# Revit family: FlushPlateControlPanel-ToiletCisterns-ProPhotocelled-Vitra-VitrAProSeries_748-1420
name_source: partatom
category: Plumbing Fixtures
revit_build: Autodesk Revit 2017 (Build: 20160225_1515(x64)
units: mm (PartAtom-declared; Revit-internal decimal feet)

## family parameters
Cut with Voids When Loaded = No
Host = Face
OmniClass Number = 23.45.00.00
OmniClass Title = Sanitary, Laundry, and Cleaning Equipment
Part Type = Normal
Room Calculation Point = No
Round Connector Dimension = Use Diameter
Shared = Yes

## types (6) — shared parameters
BIMobject category = Toilet Cisterns
Brand = VitrA
CW Connection = No
Design country = Turkey
HW Connection = No
IFC Classification = Sanitary Terminal
Main Material = Metal
Manufacturer = Vitra
Manufacturer name = Vitra
Masterformat 2014 Code = 22 00 00
Masterformat 2014 Description = Plumbing
Mounting type = Wall Mounted
NBS Referans Code = 31-75
NBS Referans Description = Sanitary Accessories
Nominal Depth (mm) = 10 mm  [stored 0.0328084 ft]
Nominal Height (mm) = 160 mm  [stored 0.524934 ft]
Nominal Width (mm) = 240 mm  [stored 0.787402 ft]
OmniClass Code = 23-31 00 00
OmniClass Description = Plumbing Specific Products and Equipment
Primary Material = Matte Black
Product Properties = Vitra Pro Control Panel
Product certification = https://www.vitraglobal.com
Product family = VitrA Pro
Product group = WC Cisterns Control Panel
UNSPSC Description = Plumbing connectors
URL = https://www.vitra.com.tr
Uniclass 1.4 Code = L71111
Uniclass 1.4 Description = Packaged plumbing units
Uniclass 2.0 Code = PR-31-75
Uniclass 2.0 Description = Sanitary Accessories
Uniclass 2015 Code = Pr_40_20_76
Uniclass 2015 Name = Sanitary accessories
Uniformat II Code = D20
Uniformat II Description = PLUMBING
Vent Connection = No
Warranty Period (Year) = 2 Years
Waste Connection = No
Weight Net (kg) = 0.95
Youtube = https://www.youtube.com
zero-valued in all types: Default Elevation

## per-type parameters (varying)
| type | Article No. (default) | Coating Material | Color | Description | Model | Product SKU | Product url | Technical description |
| FlushPlateControlPanel-ToiletCisterns-ProPhotocelled-Vitra-VitrAProSeries_748-1420IND | 748-1420IND | Gold | Gold | VitrA WC Cisterns Control Panel - Pro Photocelled Control Panel - Electronic- Gold - Compatible with Slim Frames (748-frames) | 748-1420IND | 748-1420IND | https://www.vitra-india.com | https://www.vitra-india.com |
| FlushPlateControlPanel-ToiletCisterns-ProPhotocelled-Vitra-VitrAProSeries_748-1420 | 748-1420 | Gold | Gold | VitrA WC Cisterns Control Panel - Pro Photocelled Control Panel - Electronic- Gold - Compatible with Slim Frames (748-frames) | 748-1420 | 748-1420 | https://www.vitra.com.tr | https://www.vitra.com.tr |
| FlushPlateControlPanel-ToiletCisterns-ProPhotocelled-Vitra-VitrAProSeries_748-1440 | 748-1440 | Brushed Chrome | Brushed Chrome | VitrA WC Cisterns Control Panel - Pro Photocelled Control Panel - Electronic- Brushed Chrome- Compatible with Slim Frames (748-frames) | 748-1440 | 748-1440 | https://www.vitra.com.tr | https://www.vitra.com.tr |
| FlushPlateControlPanel-ToiletCisterns-ProPhotocelled-Vitra-VitrAProSeries_748-1440IND | 748-1440IND | Brushed Chrome | Brushed Chrome | VitrA WC Cisterns Control Panel - Pro Photocelled Control Panel - Electronic- Brushed Chrome- Compatible with Slim Frames (748-frames) | 748-1440IND | 748-1440IND | https://www.vitra-india.com | https://www.vitra-india.com |
| FlushPlateControlPanel-ToiletCisterns-ProPhotocelled-Vitra-VitrAProSeries_748-1421 | 748-1421 | Polished Chrome | Polished Chrome | VitrA WC Cisterns Control Panel - Pro Photocelled Control Panel - Electronic - Chrome - Compatible with Slim Frames (748-frames) | 748-1421 | 748-1421 | https://www.vitra.com.tr | https://www.vitra.com.tr |
| FlushPlateControlPanel-ToiletCisterns-ProPhotocelled-Vitra-VitrAProSeries_748-1421IND | 748-1421IND | Polished Chrome | Polished Chrome | VitrA WC Cisterns Control Panel - Pro Photocelled Control Panel - Electronic - Chrome - Compatible with Slim Frames (748-frames) | 748-1421IND | 748-1421IND | https://www.vitra-india.com | https://www.vitra-india.com |

note: [stored X ft] marks values corroborated as IEEE doubles in the binary element streams (Revit-internal decimal feet)

## geometry (parser evidence)
native form markers: Sweep x2
no freeform markers — native parametric forms only
